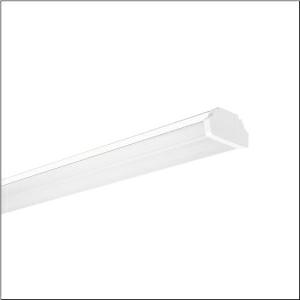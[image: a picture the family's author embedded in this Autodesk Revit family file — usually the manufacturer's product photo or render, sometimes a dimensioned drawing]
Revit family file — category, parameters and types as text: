
# Revit family: dus_31_gen_2_53bd812dv6dxd2_193c
name_source: partatom
category: Lighting Fixtures
units: mm (PartAtom-declared; Revit-internal decimal feet)

## family parameters
Cut with Voids When Loaded = No
Host = Face
Light Source = No
Part Type = Normal
Room Calculation Point = No
Round Connector Dimension = Use Diameter
Shared = No

## types (1)
- --- (1 x LED, 13280 lm, 74.9 W, 6500K)
    Apparent Load = 75 VA
    CIE Flux Codes = 47 80 95 93 100
    Color Rendering = 80
    Color Temperature = 6500K
    Default Elevation = 1800 mm
    Description = DUS 31 Gen.2, luminaire insert, of sheet steel, coil coated, white, length: 1.535mm, width: 81mm, height: 90mm, 5x system unit, system units: 307mm, LED rated luminous flux: 13.280lm, light colour: 865, SDCM (Standard Deviation of Colour Matching)MacAdam ≤ 3 SDCM (initial), control gear: DALI 2, control gear: ECG DALI, with plug, 5-pole, with phase selection, mains connection: 220..240V, AC, 50/60Hz, rated input power: 75W, through-wiring accessed according to module size, primary optical cover: cover, of PMMA, light emission: direct distribution, primary light characteristic: symmetric, protection rating (complete): IP20, protection rating (LED compartment): IP50, insulation class (complete): insulation class I (protective earthing), certification: CE, ENEC, VDE, UKCA, impact resistance: IK03, permissible ambient temperature for indoor applications: -25..+35°C, corresponds to IFS (International Featured Standards) requirements for safety and quality in the food industry, reducing of maximum allowable ambient temperature of 5°C with ceiling mounting, packaging unit: 1 piece
    Height = 95 mm
    Lamp = 1 x LED
    Lamp Light Flux = 13280 lm
    Lamp Power = 74.9 W
    Lamp count = 1
    Length = 1535 mm
    Luminous efficacy = 177 lm/W
    Manufacturer = Siteco
    ModVariant = No
    Model = 53BD812DV6DXD2
    Mounting Place = Ceiling
    Mounting Type = Pendant
    Number of Poles = 1
    OnlyDefault = Yes
    Power Factor = 1
    Product Name = DUS 31 Gen.2
    Product group = luminaire insert | ceiling pendant
    ProductGroupID = 901
    Protection Class = Protection class I
    Protection Degree = IP 20
    RLX_Detail_Level = 1
    RLX_Emergency_Light_Flux = 0 lm
    RLX_Emergency_Type = 0
    RLX_Emergency_Type_DB = No
    RlxData = <blob elided: 32205 chars, md5=dc274647>
    Socket = socket
    Standby Power = 0 W
    System Light Flux = 13280 lm
    System Power = 75 W
    Type Comments = factory setting: luminous flux: 100 % | dim-lin: 254 | 511 mA
    Type Image = l_1319596.jpg
    URL = http://relux.com
    VarID = @adj_051305
    Voltage = 0 V
    Weight = 0.00 kg
    Width = 81 mm

## geometry (parser evidence)
native form markers: Blend x4, Sweep x13
no freeform markers — native parametric forms only
